# Revit family: Faucet-Kitchen-Grohe-Defined-30377_Series
name_source: partatom
category: Plumbing Fixtures
units: mm (PartAtom-declared; Revit-internal decimal feet)

## family parameters
Always vertical = No
Cut with Voids When Loaded = No
OmniClass Number = 23.45.55.14
OmniClass Title = Single Faucets
Part Type = Normal
Room Calculation Point = No
Round Connector Dimension = Use Diameter
Shared = Yes
Work Plane-Based = Yes

## types (2) — shared parameters
ADA Compliant = Yes
Assembly Code = D2020300
CEC Compliant = Yes
CW Connection = No
CWFU = 3
CalGreen Compliant = Yes
Compliance Certifications = • ADA • CEC Certified • Low Lead Certified • CALGreen Compliant• Massachusetts Plumbing Board Approved• Energy Policy Act of 1992• NSF 372• CSA B125.1• ASME A112.18.1• Complies with lead plumbing laws
Default Elevation = 0"
Description = Single-Handle Pull Down Kitchen Faucet Dual Spray 1.75 GPM
Flow Rate = 1.75 GPM
HW Connection = No
HWFU = 3
Height = 15 9/16"
Installation Type = Surface Mounted
Length = 8 11/16"
Manufacturer = Grohe
Product Documentation Link = https://americanstandard.box.com
Product Page URL = https://www.grohe.us
Revised Date = 06/07/2023
Tempered Water Connection = Yes
Tempered Water Connection Diameter = 9/16"
URL = https://www.grohe.us
Vent Connection = No
Waste Connection = No
Width = 2 3/8"
zero-valued in all types: WFU

## per-type parameters (varying)
| type | Finish | Material |
| 30377DC0 | Brass-Grohe-DC0-SuperSteel | Brass-Grohe-DC0-SuperSteel |
| 30377000 | Brass-Grohe-000-Starlight Chrome | Brass-Grohe-000-Starlight Chrome |

note: column(s) folded — value = type name in every type: Model

## geometry (parser evidence)
native form markers: Sweep x2
no freeform markers — native parametric forms only
